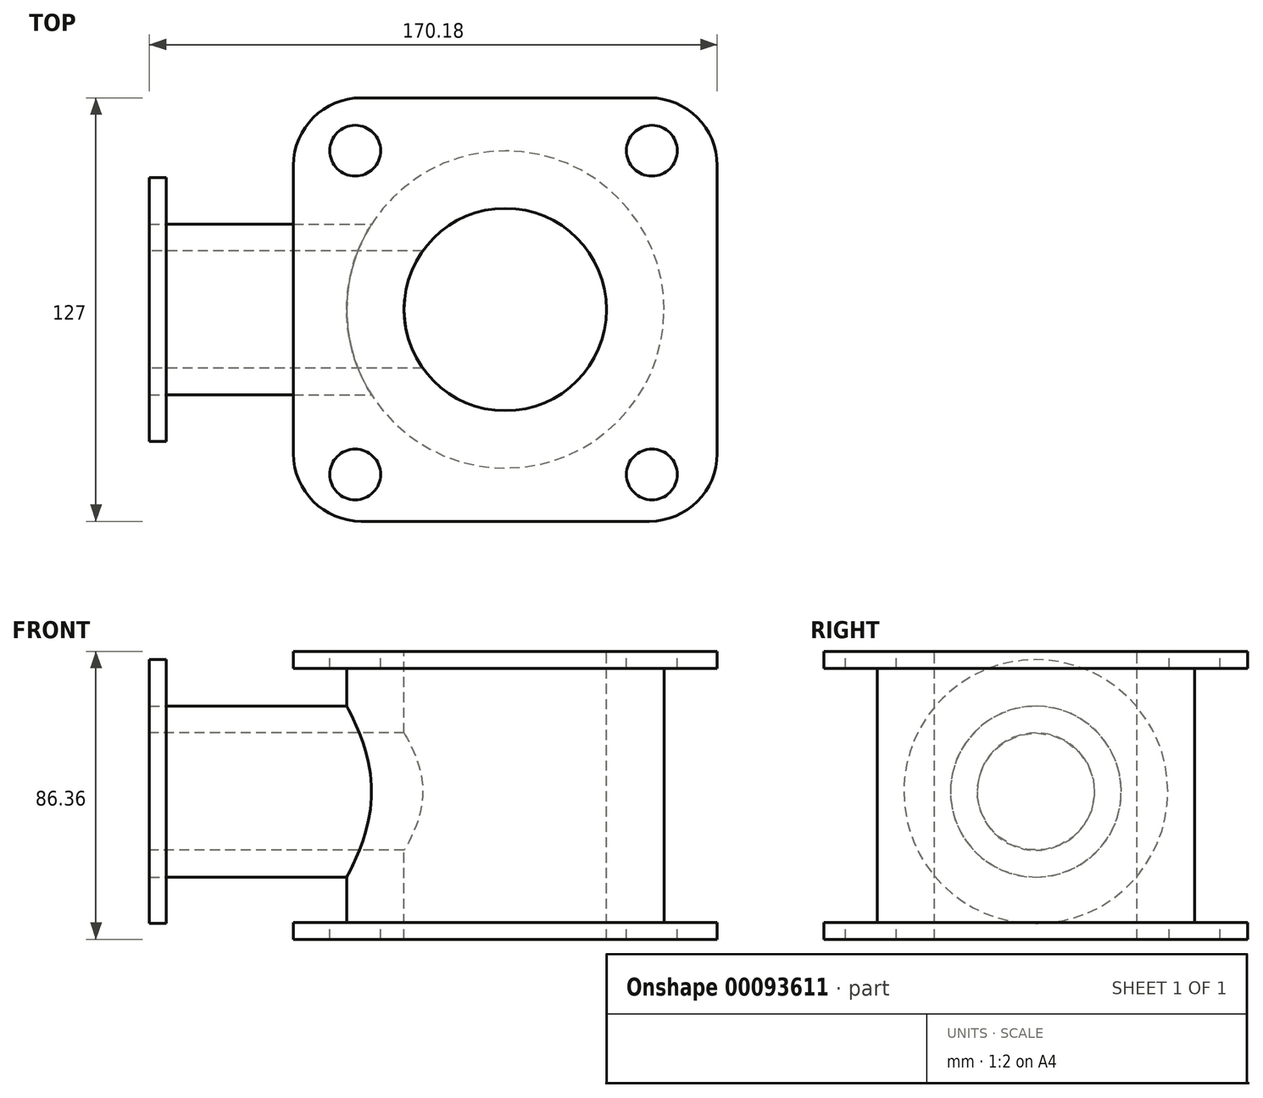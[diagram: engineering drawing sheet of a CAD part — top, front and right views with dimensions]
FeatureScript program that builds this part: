
annotation { "Feature Type Name" : "Feature", "Feature Type Description" : "" }
export const myFeature = defineFeature(function(context is Context, id is Id, definition is map)
    precondition{}
    {
        {
            var Q0;
            Q0=qCreatedBy(makeId("Top.planeOp"),FACE);
            var sketch = newSketch(context, id + "F0", { "sketchPlane" : qUnion([Q0])});
            skLineSegment(sketch, "E0", {"start": v(63.5, 0) * mm, "end": v(63.5, 63.5) * mm});
            skLineSegment(sketch, "E1", {"start": v(63.5, 63.5) * mm, "end": v(0, 63.5) * mm});
            skLineSegment(sketch, "E2.MirrorCS", {"start": v(-63.5, 63.5) * mm, "end": v(0, 63.5) * mm});
            skLineSegment(sketch, "E3.MirrorCS", {"start": v(-63.5, 0) * mm, "end": v(-63.5, 63.5) * mm});
            skLineSegment(sketch, "E4.MirrorCS", {"start": v(-63.5, 0) * mm, "end": v(-63.5, -63.5) * mm});
            skLineSegment(sketch, "E5.MirrorCS", {"start": v(-63.5, -63.5) * mm, "end": v(0, -63.5) * mm});
            skLineSegment(sketch, "E6.MirrorCS", {"start": v(63.5, -63.5) * mm, "end": v(0, -63.5) * mm});
            skLineSegment(sketch, "E7.MirrorCS", {"start": v(63.5, 0) * mm, "end": v(63.5, -63.5) * mm});
            skSolve(sketch);
        }
        {
            var Q0;
            Q0 = qSketchRegion(id + "F0", true);
            extrude(context, id + "F1", {"entities" : qUnion([Q0]), "depth" : 5.08 * mm});
        }
        {
            var Q0;
            Q0=makeQuery(id+"F1.opExtrude","CAP_FACE",FACE,{"disambiguationData":[OSD([sQuery(id+"F0.wireOp",EDGE,"E0"),sQuery(id+"F0.wireOp",EDGE,"E1"),sQuery(id+"F0.wireOp",EDGE,"E2.MirrorCS"),sQuery(id+"F0.wireOp",EDGE,"E3.MirrorCS"),sQuery(id+"F0.wireOp",EDGE,"E4.MirrorCS"),sQuery(id+"F0.wireOp",EDGE,"E5.MirrorCS"),sQuery(id+"F0.wireOp",EDGE,"E6.MirrorCS"),sQuery(id+"F0.wireOp",EDGE,"E7.MirrorCS")])],"isStart":false});
            var sketch = newSketch(context, id + "F2", { "sketchPlane" : qUnion([Q0])});
            skCircle(sketch, "E8", {"center": v(0, 0) * mm, "radius": 47.56 * mm});
            skSolve(sketch);
        }
        {
            var Q0;
            Q0=makeQuery(id+"F2.imprint","IMPRINT",FACE,{"disambiguationData":[TD([[makeQuery(id+"F2.imprint","IMPRINT",EDGE,{"derivedFrom":sQuery(id+"F2.wireOp",EDGE,"E8")}),1.0]])]});
            extrude(context, id + "F3", {"entities" : qUnion([Q0]), "operationType" : NewBodyOperationType.ADD, "depth" : 76.2 * mm});
        }
        {
            var Q0;
            Q0=makeQuery(id+"F3.opExtrude","CAP_FACE",FACE,{"disambiguationData":[OSD([sQuery(id+"F2.wireOp",EDGE,"E8")])],"isStart":false});
            var sketch = newSketch(context, id + "F4", { "sketchPlane" : qUnion([Q0])});
            skLineSegment(sketch, "E9.bottom", {"start": v(63.5, 63.5) * mm, "end": v(-63.5, 63.5) * mm});
            skLineSegment(sketch, "E9.top", {"start": v(63.5, -63.5) * mm, "end": v(-63.5, -63.5) * mm});
            skLineSegment(sketch, "E9.left", {"start": v(63.5, 63.5) * mm, "end": v(63.5, -63.5) * mm});
            skLineSegment(sketch, "E9.right", {"start": v(-63.5, 63.5) * mm, "end": v(-63.5, -63.5) * mm});
            skPoint(sketch, "E9.middle", {"position": v(0, 0) * mm});
            skSolve(sketch);
        }
        {
            var Q0;
            Q0 = qSketchRegion(id + "F4", true);
            extrude(context, id + "F5", {"entities" : qUnion([Q0]), "operationType" : NewBodyOperationType.ADD, "depth" : 5.08 * mm});
        }
        {
            var Q0;
            Q0=makeQuery(id+"F1.opExtrude","SWEPT_EDGE",EDGE,{"disambiguationData":[OSD([sQuery(id+"F0.wireOp",EDGE,"E2.MirrorCS"),sQuery(id+"F0.wireOp",EDGE,"E3.MirrorCS")])]});
            var Q1;
            Q1=makeQuery(id+"F5.opExtrude","SWEPT_EDGE",EDGE,{"disambiguationData":[OSD([sQuery(id+"F4.wireOp",EDGE,"E9.bottom"),sQuery(id+"F4.wireOp",EDGE,"E9.right")])]});
            var Q2;
            Q2=makeQuery(id+"F5.opExtrude","SWEPT_EDGE",EDGE,{"disambiguationData":[OSD([sQuery(id+"F4.wireOp",EDGE,"E9.bottom"),sQuery(id+"F4.wireOp",EDGE,"E9.left")])]});
            var Q3;
            Q3=makeQuery(id+"F1.opExtrude","SWEPT_EDGE",EDGE,{"disambiguationData":[OSD([sQuery(id+"F0.wireOp",EDGE,"E0"),sQuery(id+"F0.wireOp",EDGE,"E1")])]});
            var Q4;
            Q4=makeQuery(id+"F1.opExtrude","SWEPT_EDGE",EDGE,{"disambiguationData":[OSD([sQuery(id+"F0.wireOp",EDGE,"E6.MirrorCS"),sQuery(id+"F0.wireOp",EDGE,"E7.MirrorCS")])]});
            var Q5;
            Q5=makeQuery(id+"F5.opExtrude","SWEPT_EDGE",EDGE,{"disambiguationData":[OSD([sQuery(id+"F4.wireOp",EDGE,"E9.top"),sQuery(id+"F4.wireOp",EDGE,"E9.left")])]});
            var Q6;
            Q6=makeQuery(id+"F5.opExtrude","SWEPT_EDGE",EDGE,{"disambiguationData":[OSD([sQuery(id+"F4.wireOp",EDGE,"E9.top"),sQuery(id+"F4.wireOp",EDGE,"E9.right")])]});
            var Q7;
            Q7=makeQuery(id+"F1.opExtrude","SWEPT_EDGE",EDGE,{"disambiguationData":[OSD([sQuery(id+"F0.wireOp",EDGE,"E4.MirrorCS"),sQuery(id+"F0.wireOp",EDGE,"E5.MirrorCS")])]});
            fillet(context, id + "F6", {"entities" : qUnion([Q0, Q1, Q2, Q3, Q4, Q5, Q6, Q7]), "radius" : 20.32 * mm, "tangentPropagation" : true, "allowEdgeOverflow" : false});
        }
        {
            var Q0;
            Q0=qCreatedBy(makeId("Right.planeOp"),FACE);
            var sketch = newSketch(context, id + "F7", { "sketchPlane" : qUnion([Q0])});
            skCircle(sketch, "E10", {"center": v(0, 44.28) * mm, "radius": 25.62 * mm});
            skSolve(sketch);
        }
        {
            var Q0;
            Q0 = qSketchRegion(id + "F7", true);
            extrude(context, id + "F8", {"entities" : qUnion([Q0]), "operationType" : NewBodyOperationType.ADD, "oppositeDirection" : true, "depth" : 106.68 * mm});
        }
        {
            var Q0;
            Q0=makeQuery(id+"F8.opExtrude","CAP_FACE",FACE,{"disambiguationData":[OSD([sQuery(id+"F7.wireOp",EDGE,"E10")])],"isStart":false});
            var sketch = newSketch(context, id + "F9", { "sketchPlane" : qUnion([Q0])});
            skCircle(sketch, "E11", {"center": v(0, 44.28) * mm, "radius": 39.55 * mm});
            skSolve(sketch);
        }
        {
            var Q0;
            Q0=makeQuery(id+"F9.imprint","IMPRINT",FACE,{"disambiguationData":[TD([[makeQuery(id+"F9.imprint","IMPRINT",EDGE,{"derivedFrom":sQuery(id+"F9.wireOp",EDGE,"E11")}),1.0]])]});
            extrude(context, id + "F10", {"entities" : qUnion([Q0]), "oppositeDirection" : true, "depth" : 5.08 * mm});
        }
        {
            var Q0;
            Q0=makeQuery(id+"F5.opExtrude","CAP_FACE",FACE,{"disambiguationData":[OSD([sQuery(id+"F4.wireOp",EDGE,"E9.bottom"),sQuery(id+"F4.wireOp",EDGE,"E9.top"),sQuery(id+"F4.wireOp",EDGE,"E9.left"),sQuery(id+"F4.wireOp",EDGE,"E9.right")])],"isStart":false});
            var sketch = newSketch(context, id + "F11", { "sketchPlane" : qUnion([Q0])});
            skPoint(sketch, "E12", {"position": v(-45, 47.64) * mm});
            skPoint(sketch, "E13", {"position": v(43.93, 47.64) * mm});
            skPoint(sketch, "E14", {"position": v(43.93, -49.46) * mm});
            skPoint(sketch, "E15", {"position": v(-45, -49.46) * mm});
            skSolve(sketch);
        }
        {
            var Q0;
            Q0=sQuery(id+"F11.wireOp",VERTEX,"E12");
            var Q1;
            Q1=sQuery(id+"F11.wireOp",VERTEX,"E13");
            var Q2;
            Q2=sQuery(id+"F11.wireOp",VERTEX,"E14");
            var Q3;
            Q3=sQuery(id+"F11.wireOp",VERTEX,"E15");
            var Q4;
            Q4=makeQuery(id+"F1.opExtrude","SWEPT_BODY",BODY,{"disambiguationData":[OSD([sQuery(id+"F0.wireOp",EDGE,"E0"),sQuery(id+"F0.wireOp",EDGE,"E1"),sQuery(id+"F0.wireOp",EDGE,"E2.MirrorCS"),sQuery(id+"F0.wireOp",EDGE,"E3.MirrorCS"),sQuery(id+"F0.wireOp",EDGE,"E4.MirrorCS"),sQuery(id+"F0.wireOp",EDGE,"E5.MirrorCS"),sQuery(id+"F0.wireOp",EDGE,"E6.MirrorCS"),sQuery(id+"F0.wireOp",EDGE,"E7.MirrorCS")])]});
            hole(context, id + "F12", {"style" : HoleStyle.SIMPLE, "endStyle" : HoleEndStyle.THROUGH, "holeDiameter" : 15.24 * mm, "locations" : qUnion([Q0, Q1, Q2, Q3]), "scope" : qUnion([Q4]), "isTappedThrough" : true});
        }
        {
            var Q0;
            Q0=makeQuery(id+"F5.opExtrude","CAP_FACE",FACE,{"disambiguationData":[OSD([sQuery(id+"F4.wireOp",EDGE,"E9.bottom"),sQuery(id+"F4.wireOp",EDGE,"E9.top"),sQuery(id+"F4.wireOp",EDGE,"E9.left"),sQuery(id+"F4.wireOp",EDGE,"E9.right")])],"isStart":false});
            var sketch = newSketch(context, id + "F13", { "sketchPlane" : qUnion([Q0])});
            skCircle(sketch, "E16", {"center": v(0, 0) * mm, "radius": 30.34 * mm});
            skSolve(sketch);
        }
        {
            var Q0;
            Q0 = qSketchRegion(id + "F13", true);
            extrude(context, id + "F14", {"entities" : qUnion([Q0]), "operationType" : NewBodyOperationType.REMOVE, "oppositeDirection" : true, "depth" : 254 * mm});
        }
        {
            var Q0;
            Q0=makeQuery(id+"F8.opExtrude","CAP_FACE",FACE,{"disambiguationData":[OSD([sQuery(id+"F7.wireOp",EDGE,"E10")])],"isStart":false});
            var sketch = newSketch(context, id + "F15", { "sketchPlane" : qUnion([Q0])});
            skCircle(sketch, "E17", {"center": v(0, 44.28) * mm, "radius": 17.58 * mm});
            skSolve(sketch);
        }
        {
            var Q0;
            Q0 = qSketchRegion(id + "F15", true);
            extrude(context, id + "F16", {"entities" : qUnion([Q0]), "operationType" : NewBodyOperationType.REMOVE, "oppositeDirection" : true, "depth" : 101.6 * mm});
        }
    });
